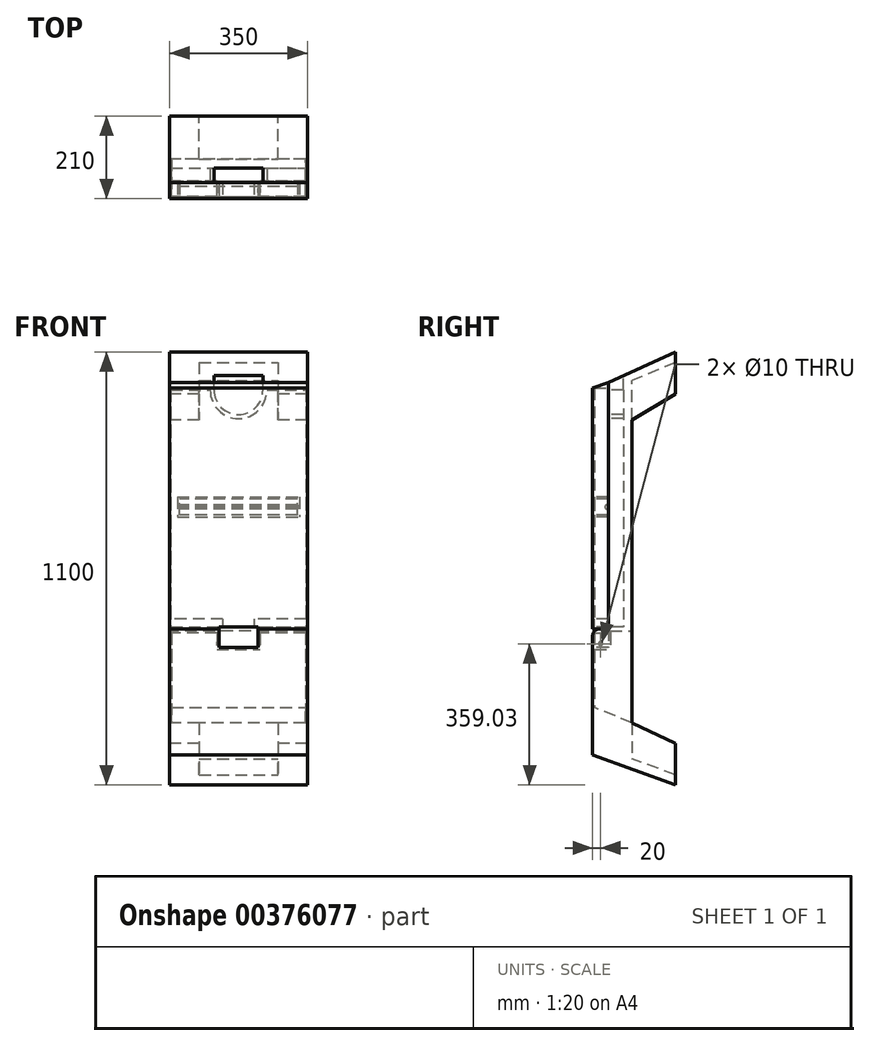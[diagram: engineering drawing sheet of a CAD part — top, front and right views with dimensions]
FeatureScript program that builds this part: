
annotation { "Feature Type Name" : "Feature", "Feature Type Description" : "" }
export const myFeature = defineFeature(function(context is Context, id is Id, definition is map)
    precondition{}
    {
        {
            var Q0;
            Q0=qCreatedBy(makeId("Front.planeOp"),FACE);
            var sketch = newSketch(context, id + "F0", { "sketchPlane" : qUnion([Q0])});
            skLineSegment(sketch, "E0.bottom", {"start": v(175, -310) * mm, "end": v(-175, -310) * mm});
            skLineSegment(sketch, "E0.top", {"start": v(175, 364) * mm, "end": v(-175, 364) * mm});
            skLineSegment(sketch, "E0.left", {"start": v(175, -310) * mm, "end": v(175, 364) * mm});
            skLineSegment(sketch, "E0.right", {"start": v(-175, -310) * mm, "end": v(-175, 364) * mm});
            skSolve(sketch);
        }
        {
            var Q0;
            Q0=makeQuery(id+"F0.imprint","IMPRINT",FACE,{"disambiguationData":[TD([[makeQuery(id+"F0.imprint","IMPRINT",EDGE,{"derivedFrom":sQuery(id+"F0.wireOp",EDGE,"E0.bottom")}),-1.0]])]});
            extrude(context, id + "F1", {"entities" : qUnion([Q0]), "depth" : 40 * mm});
        }
        {
            var Q0;
            Q0=makeQuery(id+"F1.opExtrude","CAP_FACE",FACE,{"disambiguationData":[OSD([sQuery(id+"F0.wireOp",EDGE,"E0.bottom"),sQuery(id+"F0.wireOp",EDGE,"E0.top"),sQuery(id+"F0.wireOp",EDGE,"E0.left"),sQuery(id+"F0.wireOp",EDGE,"E0.right")])],"isStart":true});
            var sketch = newSketch(context, id + "F2", { "sketchPlane" : qUnion([Q0])});
            skLineSegment(sketch, "E1.bottom", {"start": v(-172, 349) * mm, "end": v(172, 349) * mm});
            skLineSegment(sketch, "E1.top", {"start": v(-172, -237.6) * mm, "end": v(172, -237.6) * mm});
            skLineSegment(sketch, "E1.left", {"start": v(-172, 349) * mm, "end": v(-172, -237.6) * mm});
            skLineSegment(sketch, "E1.right", {"start": v(172, 349) * mm, "end": v(172, -237.6) * mm});
            skSolve(sketch);
        }
        {
            var Q0;
            Q0 = qSketchRegion(id + "F2", true);
            extrude(context, id + "F3", {"entities" : qUnion([Q0]), "operationType" : NewBodyOperationType.REMOVE, "oppositeDirection" : true, "depth" : 36 * mm});
        }
        {
            var Q0;
            Q0=makeQuery(id+"F3.boolean.opBoolean","COPY",FACE,{"derivedFrom":makeQuery(id+"F3.opExtrude","CAP_FACE",FACE,{"disambiguationData":[OSD([sQuery(id+"F2.wireOp",EDGE,"E1.bottom"),sQuery(id+"F2.wireOp",EDGE,"E1.top"),sQuery(id+"F2.wireOp",EDGE,"E1.left"),sQuery(id+"F2.wireOp",EDGE,"E1.right")])],"isStart":false})});
            var sketch = newSketch(context, id + "F4", { "sketchPlane" : qUnion([Q0])});
            skLineSegment(sketch, "E2.bottom", {"start": v(155, 72.4) * mm, "end": v(-155, 72.4) * mm});
            skLineSegment(sketch, "E2.top", {"start": v(155, 22.4) * mm, "end": v(-155, 22.4) * mm});
            skLineSegment(sketch, "E2.left", {"start": v(155, 72.4) * mm, "end": v(155, 22.4) * mm});
            skLineSegment(sketch, "E2.right", {"start": v(-155, 72.4) * mm, "end": v(-155, 22.4) * mm});
            skLineSegment(sketch, "E3.bottom", {"start": v(150, 67.4) * mm, "end": v(-150, 67.4) * mm});
            skLineSegment(sketch, "E3.top", {"start": v(150, 27.4) * mm, "end": v(-150, 27.4) * mm});
            skLineSegment(sketch, "E3.left", {"start": v(150, 67.4) * mm, "end": v(150, 27.4) * mm});
            skLineSegment(sketch, "E3.right", {"start": v(-150, 67.4) * mm, "end": v(-150, 27.4) * mm});
            skSolve(sketch);
        }
        {
            var Q0;
            Q0 = qSketchRegion(id + "F4", true);
            extrude(context, id + "F5", {"entities" : qUnion([Q0]), "operationType" : NewBodyOperationType.ADD, "depth" : 37 * mm});
        }
        {
            var Q0;
            Q0=qCreatedBy(makeId("Right.planeOp"),FACE);
            var sketch = newSketch(context, id + "F6", { "sketchPlane" : qUnion([Q0])});
            skCircle(sketch, "E4", {"center": v(-4, 47.4) * mm, "radius": 5 * mm});
            skSolve(sketch);
        }
        {
            var Q0;
            Q0 = qSketchRegion(id + "F6", true);
            extrude(context, id + "F7", {"entities" : qUnion([Q0]), "endBound" : BoundingType.SYMMETRIC, "depth" : 300 * mm});
        }
        {
            var Q0;
            Q0=makeQuery(id+"F1.opExtrude","CAP_FACE",FACE,{"disambiguationData":[OSD([sQuery(id+"F0.wireOp",EDGE,"E0.bottom"),sQuery(id+"F0.wireOp",EDGE,"E0.top"),sQuery(id+"F0.wireOp",EDGE,"E0.left"),sQuery(id+"F0.wireOp",EDGE,"E0.right")])],"isStart":true});
            var sketch = newSketch(context, id + "F8", { "sketchPlane" : qUnion([Q0])});
            skLineSegment(sketch, "E5.bottom", {"start": v(-175, -262.6) * mm, "end": v(-50, -262.6) * mm});
            skLineSegment(sketch, "E5.top", {"start": v(-175, -342.73) * mm, "end": v(-50, -342.73) * mm});
            skLineSegment(sketch, "E5.left", {"start": v(-175, -262.6) * mm, "end": v(-175, -342.73) * mm});
            skLineSegment(sketch, "E5.right", {"start": v(-50, -262.6) * mm, "end": v(-50, -342.73) * mm});
            skLineSegment(sketch, "E6.bottom", {"start": v(175, -262.6) * mm, "end": v(50, -262.6) * mm});
            skLineSegment(sketch, "E6.top", {"start": v(175, -338.6) * mm, "end": v(50, -338.6) * mm});
            skLineSegment(sketch, "E6.left", {"start": v(175, -262.6) * mm, "end": v(175, -338.6) * mm});
            skLineSegment(sketch, "E6.right", {"start": v(50, -262.6) * mm, "end": v(50, -338.6) * mm});
            skSolve(sketch);
        }
        {
            var Q0;
            Q0 = qSketchRegion(id + "F8", true);
            extrude(context, id + "F9", {"entities" : qUnion([Q0]), "operationType" : NewBodyOperationType.REMOVE, "endBound" : BoundingType.THROUGH_ALL, "oppositeDirection" : true, "depth" : 25 * mm});
        }
        {
            var Q0;
            Q0=makeQuery(id+"F1.opExtrude","CAP_EDGE",EDGE,{"disambiguationData":[OSD([sQuery(id+"F0.wireOp",EDGE,"E0.bottom")])],"isStart":true});
            fillet(context, id + "F10", {"entities" : qUnion([Q0]), "radius" : 20 * mm, "tangentPropagation" : true, "allowEdgeOverflow" : false});
        }
        {
            var Q0;
            Q0=makeQuery(id+"F9.boolean.opBoolean","COPY",FACE,{"derivedFrom":makeQuery(id+"F9.opExtrude","SWEPT_FACE",FACE,{"disambiguationData":[OSD([sQuery(id+"F8.wireOp",EDGE,"E5.right")])]})});
            var sketch = newSketch(context, id + "F11", { "sketchPlane" : qUnion([Q0])});
            skCircle(sketch, "E7", {"center": v(-20, -300) * mm, "radius": 5 * mm});
            skSolve(sketch);
        }
        {
            var Q0;
            Q0 = qSketchRegion(id + "F11", true);
            extrude(context, id + "F12", {"entities" : qUnion([Q0]), "operationType" : NewBodyOperationType.ADD, "depth" : 25 * mm});
        }
        {
            var Q0;
            Q0=makeQuery(id+"F9.boolean.opBoolean","COPY",FACE,{"derivedFrom":makeQuery(id+"F9.opExtrude","SWEPT_FACE",FACE,{"disambiguationData":[OSD([sQuery(id+"F8.wireOp",EDGE,"E6.right")])]})});
            var sketch = newSketch(context, id + "F13", { "sketchPlane" : qUnion([Q0])});
            skCircle(sketch, "E8.0", {"center": v(20, -300) * mm, "radius": 5 * mm});
            skSolve(sketch);
        }
        {
            var Q0;
            Q0 = qSketchRegion(id + "F13", true);
            extrude(context, id + "F14", {"entities" : qUnion([Q0]), "operationType" : NewBodyOperationType.ADD, "depth" : 25 * mm});
        }
        {
            var Q0;
            Q0=makeQuery(id+"F1.opExtrude","SWEPT_FACE",FACE,{"disambiguationData":[OSD([sQuery(id+"F0.wireOp",EDGE,"E0.right")])]});
            var sketch = newSketch(context, id + "F15", { "sketchPlane" : qUnion([Q0])});
            skLineSegment(sketch, "E9", {"start": v(0, 364) * mm, "end": v(40, 349) * mm});
            skLineSegment(sketch, "E10.0", {"start": v(40, 364) * mm, "end": v(0, 364) * mm});
            skLineSegment(sketch, "E11.0", {"start": v(40, 349) * mm, "end": v(40, 364) * mm});
            skPoint(sketch, "E12.orphan", {"position": v(40, -262.6) * mm});
            skSolve(sketch);
        }
        {
            var Q0;
            Q0 = qSketchRegion(id + "F15", true);
            extrude(context, id + "F16", {"entities" : qUnion([Q0]), "operationType" : NewBodyOperationType.REMOVE, "endBound" : BoundingType.THROUGH_ALL, "oppositeDirection" : true, "depth" : 25 * mm});
        }
        {
            var Q0;
            Q0=makeQuery(id+"F1.opExtrude","CAP_FACE",FACE,{"disambiguationData":[OSD([sQuery(id+"F0.wireOp",EDGE,"E0.bottom"),sQuery(id+"F0.wireOp",EDGE,"E0.top"),sQuery(id+"F0.wireOp",EDGE,"E0.left"),sQuery(id+"F0.wireOp",EDGE,"E0.right")])],"isStart":true});
            var sketch = newSketch(context, id + "F17", { "sketchPlane" : qUnion([Q0])});
            skLineSegment(sketch, "E13.bottom", {"start": v(-40, -195.53) * mm, "end": v(40, -195.53) * mm});
            skLineSegment(sketch, "E13.top", {"start": v(-40, -275) * mm, "end": v(40, -275) * mm});
            skLineSegment(sketch, "E13.left", {"start": v(-40, -195.53) * mm, "end": v(-40, -275) * mm});
            skLineSegment(sketch, "E13.right", {"start": v(40, -195.53) * mm, "end": v(40, -275) * mm});
            skSolve(sketch);
        }
        {
            var Q0;
            Q0 = qSketchRegion(id + "F17", true);
            var Q1;
            {var subQ0=sQuery(id+"F2.wireOp",EDGE,"E1.right");var subQ1=sQuery(id+"F2.wireOp",EDGE,"E1.left");var subQ2=sQuery(id+"F2.wireOp",EDGE,"E1.top");var subQ3=sQuery(id+"F2.wireOp",EDGE,"E1.bottom");Q1=makeQuery(id+"F5.boolean.opBoolean","SPLIT",FACE,{"disambiguationData":[TD([makeQuery(id+"F3.boolean.opBoolean","COPY",FACE,{"derivedFrom":makeQuery(id+"F3.opExtrude","SWEPT_FACE",FACE,{"disambiguationData":[OSD([subQ3])]})})])],"derivedFrom":makeQuery(id+"F3.boolean.opBoolean","COPY",FACE,{"derivedFrom":makeQuery(id+"F3.opExtrude","CAP_FACE",FACE,{"disambiguationData":[OSD([subQ3,subQ2,subQ1,subQ0])],"isStart":false})})});}
            extrude(context, id + "F18", {"entities" : qUnion([Q0]), "operationType" : NewBodyOperationType.REMOVE, "endBound" : BoundingType.UP_TO_SURFACE, "oppositeDirection" : true, "endBoundEntityFace" : qUnion([Q1]), "depth" : 25 * mm});
        }
        {
            var Q0;
            Q0=qCreatedBy(makeId("Right.planeOp"),FACE);
            var sketch = newSketch(context, id + "F19", { "sketchPlane" : qUnion([Q0])});
            skPoint(sketch, "E14.0", {"position": v(-40, -310) * mm});
            skPoint(sketch, "E15.0", {"position": v(-40, -262.6) * mm});
            skPoint(sketch, "E16.0", {"position": v(0, -262.6) * mm});
            skPoint(sketch, "E17.0", {"position": v(0, 364) * mm});
            skLineSegment(sketch, "E18", {"start": v(170, -659.03) * mm, "end": v(-40, -582.6) * mm});
            skLineSegment(sketch, "E19", {"start": v(-40, -582.6) * mm, "end": v(-40, -262.6) * mm});
            skLineSegment(sketch, "E20", {"start": v(0, -262.6) * mm, "end": v(-40, -262.6) * mm});
            skLineSegment(sketch, "E21", {"start": v(0, -262.6) * mm, "end": v(0, 364) * mm});
            skLineSegment(sketch, "E22", {"start": v(0, 364) * mm, "end": v(170, 440.97) * mm});
            skLineSegment(sketch, "E23", {"start": v(170, 440.97) * mm, "end": v(170, 334.97) * mm});
            skLineSegment(sketch, "E24", {"start": v(170, 334.97) * mm, "end": v(60, 268.26) * mm});
            skLineSegment(sketch, "E25", {"start": v(60, 268.26) * mm, "end": v(60, -501.74) * mm});
            skLineSegment(sketch, "E26", {"start": v(60, -501.74) * mm, "end": v(170, -553.03) * mm});
            skLineSegment(sketch, "E27", {"start": v(170, -553.03) * mm, "end": v(170, -659.03) * mm});
            skSolve(sketch);
        }
        {
            var Q0;
            Q0=makeQuery(id+"F19.imprint","IMPRINT",FACE,{"disambiguationData":[TD([[makeQuery(id+"F19.imprint","IMPRINT",EDGE,{"derivedFrom":sQuery(id+"F19.wireOp",EDGE,"E18")}),-1.0]])]});
            extrude(context, id + "F20", {"entities" : qUnion([Q0]), "endBound" : BoundingType.SYMMETRIC, "depth" : 350 * mm});
        }
        {
            var Q0;
            Q0=makeQuery(id+"F20.opExtrude","SWEPT_FACE",FACE,{"disambiguationData":[OSD([sQuery(id+"F19.wireOp",EDGE,"E21")])]});
            var sketch = newSketch(context, id + "F21", { "sketchPlane" : qUnion([Q0])});
            skLineSegment(sketch, "E28.bottom", {"start": v(-172, 344) * mm, "end": v(-72, 344) * mm});
            skLineSegment(sketch, "E28.top", {"start": v(-172, -257.6) * mm, "end": v(172, -257.6) * mm});
            skLineSegment(sketch, "E28.left", {"start": v(-172, 344) * mm, "end": v(-172, -257.6) * mm});
            skLineSegment(sketch, "E28.right", {"start": v(172, 344) * mm, "end": v(172, -257.6) * mm});
            skArc(sketch, "E29", {"start": v(-72, 344) * mm, "mid": v(0, 272) * mm, "end": v(72, 344) * mm});
            skLineSegment(sketch, "E30.trimOffspring", {"start": v(72, 344) * mm, "end": v(172, 344) * mm});
            skSolve(sketch);
        }
        {
            var Q0;
            Q0 = qSketchRegion(id + "F21", true);
            extrude(context, id + "F22", {"entities" : qUnion([Q0]), "operationType" : NewBodyOperationType.REMOVE, "oppositeDirection" : true, "depth" : 38 * mm});
        }
        {
            var Q0;
            Q0=makeQuery(id+"F20.opExtrude","SWEPT_FACE",FACE,{"disambiguationData":[OSD([sQuery(id+"F19.wireOp",EDGE,"E21")])]});
            var sketch = newSketch(context, id + "F23", { "sketchPlane" : qUnion([Q0])});
            skPoint(sketch, "E31.0", {"position": v(72, 344) * mm});
            skPoint(sketch, "E31.1", {"position": v(-72, 344) * mm});
            skArc(sketch, "E32", {"start": v(-62, 344) * mm, "mid": v(0, 282) * mm, "end": v(62, 344) * mm});
            skLineSegment(sketch, "E33.top", {"start": v(62, 388.11) * mm, "end": v(-62, 388.11) * mm});
            skLineSegment(sketch, "E33.left", {"start": v(62, 344) * mm, "end": v(62, 388.11) * mm});
            skLineSegment(sketch, "E33.right", {"start": v(-62, 344) * mm, "end": v(-62, 388.11) * mm});
            skSolve(sketch);
        }
        {
            var Q0;
            Q0 = qSketchRegion(id + "F23", true);
            extrude(context, id + "F24", {"entities" : qUnion([Q0]), "operationType" : NewBodyOperationType.REMOVE, "oppositeDirection" : true, "depth" : 38 * mm});
        }
        {
            var Q0;
            Q0=qCreatedBy(makeId("Right.planeOp"),FACE);
            var sketch = newSketch(context, id + "F25", { "sketchPlane" : qUnion([Q0])});
            skLineSegment(sketch, "E34.0", {"start": v(170, -553.03) * mm, "end": v(170, -633.03) * mm});
            skLineSegment(sketch, "E35", {"start": v(170, -633.03) * mm, "end": v(60, -593) * mm});
            skPoint(sketch, "E36.0", {"position": v(60, -501.74) * mm});
            skLineSegment(sketch, "E37", {"start": v(60, -501.74) * mm, "end": v(60, -593) * mm});
            skLineSegment(sketch, "E38", {"start": v(170, -633.03) * mm, "end": v(170, -466.14) * mm});
            skLineSegment(sketch, "E39", {"start": v(170, -466.14) * mm, "end": v(60, -501.74) * mm});
            skPoint(sketch, "E40.0.end.orphan", {"position": v(-40, -582.6) * mm});
            skPoint(sketch, "E41.orphan", {"position": v(170, -659.03) * mm});
            skPoint(sketch, "E42.0", {"position": v(170, 440.97) * mm});
            skPoint(sketch, "E42.1", {"position": v(170, 334.97) * mm});
            skPoint(sketch, "E42.2", {"position": v(60, 268.26) * mm});
            skLineSegment(sketch, "E43.0", {"start": v(170, 414.97) * mm, "end": v(170, 334.97) * mm});
            skLineSegment(sketch, "E44", {"start": v(170, 414.97) * mm, "end": v(60, 368.4) * mm});
            skLineSegment(sketch, "E45", {"start": v(170, 414.97) * mm, "end": v(170, 214.7) * mm});
            skLineSegment(sketch, "E46", {"start": v(170, 214.7) * mm, "end": v(60, 268.26) * mm});
            skLineSegment(sketch, "E47", {"start": v(60, 268.26) * mm, "end": v(60, 368.4) * mm});
            skPoint(sketch, "E48.orphan", {"position": v(0, 364) * mm});
            skSolve(sketch);
        }
        {
            var Q0;
            Q0 = qSketchRegion(id + "F25", true);
            extrude(context, id + "F26", {"entities" : qUnion([Q0]), "operationType" : NewBodyOperationType.REMOVE, "endBound" : BoundingType.SYMMETRIC, "oppositeDirection" : true, "depth" : 200 * mm});
        }
        {
            var Q0;
            Q0=qCreatedBy(makeId("Right.planeOp"),FACE);
            var sketch = newSketch(context, id + "F27", { "sketchPlane" : qUnion([Q0])});
            skPoint(sketch, "E49.0", {"position": v(0, -257.6) * mm});
            skPoint(sketch, "E50.0", {"position": v(-40, -310) * mm});
            skLineSegment(sketch, "E51.bottom", {"start": v(0, -257.6) * mm, "end": v(-40, -257.6) * mm});
            skLineSegment(sketch, "E51.top", {"start": v(0, -310) * mm, "end": v(-40, -310) * mm});
            skLineSegment(sketch, "E51.left", {"start": v(0, -257.6) * mm, "end": v(0, -310) * mm});
            skLineSegment(sketch, "E51.right", {"start": v(-40, -257.6) * mm, "end": v(-40, -310) * mm});
            skSolve(sketch);
        }
        {
            var Q0;
            Q0 = qSketchRegion(id + "F27", true);
            extrude(context, id + "F28", {"entities" : qUnion([Q0]), "operationType" : NewBodyOperationType.REMOVE, "endBound" : BoundingType.SYMMETRIC, "oppositeDirection" : true, "depth" : 100 * mm});
        }
        {
            var Q0;
            Q0=qCreatedBy(makeId("Right.planeOp"),FACE);
            var sketch = newSketch(context, id + "F29", { "sketchPlane" : qUnion([Q0])});
            skPoint(sketch, "E52.0", {"position": v(38, -257.6) * mm});
            skPoint(sketch, "E53.0", {"position": v(0, -257.6) * mm});
            skPoint(sketch, "E54.0", {"position": v(0, -310) * mm});
            skPoint(sketch, "E55.0", {"position": v(-40, -310) * mm});
            skLineSegment(sketch, "E56.bottom", {"start": v(5, -267.6) * mm, "end": v(81.3, -267.6) * mm});
            skLineSegment(sketch, "E56.left", {"start": v(5, -267.6) * mm, "end": v(5, -315) * mm});
            skLineSegment(sketch, "E56.right", {"start": v(81.3, -267.6) * mm, "end": v(81.3, -331.9) * mm});
            skLineSegment(sketch, "E57.0", {"start": v(-40, -310) * mm, "end": v(-40, -262.6) * mm});
            skLineSegment(sketch, "E58.bottom", {"start": v(-35, -315) * mm, "end": v(5, -315) * mm});
            skLineSegment(sketch, "E58.left", {"start": v(-35, -315) * mm, "end": v(-35, -462.44) * mm});
            skLineSegment(sketch, "E59", {"start": v(60, -501.74) * mm, "end": v(-35, -462.44) * mm});
            skPoint(sketch, "E60.orphan", {"position": v(-40, -582.6) * mm});
            skLineSegment(sketch, "E61", {"start": v(60, -501.74) * mm, "end": v(81.3, -331.9) * mm});
            skSolve(sketch);
        }
        {
            var Q0;
            Q0 = qSketchRegion(id + "F29", true);
            extrude(context, id + "F30", {"entities" : qUnion([Q0]), "operationType" : NewBodyOperationType.REMOVE, "endBound" : BoundingType.SYMMETRIC, "oppositeDirection" : true, "depth" : 340 * mm});
        }
        {
            var Q0;
            Q0=makeQuery(id+"F30.boolean.opBoolean","COPY",FACE,{"derivedFrom":makeQuery(id+"F30.opExtrude","SWEPT_FACE",FACE,{"disambiguationData":[OSD([sQuery(id+"F29.wireOp",EDGE,"E56.left")])]})});
            var sketch = newSketch(context, id + "F31", { "sketchPlane" : qUnion([Q0])});
            skPoint(sketch, "E62.0", {"position": v(-170, -267.6) * mm});
            skPoint(sketch, "E63.0", {"position": v(-170, -315) * mm});
            skLineSegment(sketch, "E64.top", {"start": v(-170, -315) * mm, "end": v(-55, -315) * mm});
            skLineSegment(sketch, "E64.left", {"start": v(-170, -272.6) * mm, "end": v(-170, -315) * mm});
            skLineSegment(sketch, "E64.right", {"start": v(-55, -272.6) * mm, "end": v(-55, -315) * mm});
            skPoint(sketch, "E65.0", {"position": v(170, -267.6) * mm});
            skPoint(sketch, "E65.1", {"position": v(170, -315) * mm});
            skLineSegment(sketch, "E66.top", {"start": v(170, -315) * mm, "end": v(55, -315) * mm});
            skLineSegment(sketch, "E66.left", {"start": v(170, -272.6) * mm, "end": v(170, -315) * mm});
            skLineSegment(sketch, "E66.right", {"start": v(55, -272.6) * mm, "end": v(55, -315) * mm});
            skLineSegment(sketch, "E67", {"start": v(55, -272.6) * mm, "end": v(170, -272.6) * mm});
            skLineSegment(sketch, "E68", {"start": v(-170, -272.6) * mm, "end": v(-55, -272.6) * mm});
            skSolve(sketch);
        }
        {
            var Q0;
            Q0 = qSketchRegion(id + "F31", true);
            var Q1;
            Q1=makeQuery(id+"F30.boolean.opBoolean","COPY",FACE,{"derivedFrom":makeQuery(id+"F30.opExtrude","SWEPT_FACE",FACE,{"disambiguationData":[OSD([sQuery(id+"F29.wireOp",EDGE,"E58.left")])]})});
            extrude(context, id + "F32", {"entities" : qUnion([Q0]), "operationType" : NewBodyOperationType.REMOVE, "endBound" : BoundingType.UP_TO_SURFACE, "oppositeDirection" : true, "endBoundEntityFace" : qUnion([Q1]), "depth" : 25 * mm});
        }
        {
            var Q0;
            Q0=makeQuery(id+"F32.boolean.opBoolean","COPY",FACE,{"derivedFrom":makeQuery(id+"F32.opExtrude","SWEPT_FACE",FACE,{"disambiguationData":[OSD([sQuery(id+"F31.wireOp",EDGE,"E64.right")])]})});
            var sketch = newSketch(context, id + "F33", { "sketchPlane" : qUnion([Q0])});
            skCircle(sketch, "E69.0.0", {"center": v(-20, -300) * mm, "radius": 5 * mm});
            skSolve(sketch);
        }
        {
            var Q0;
            Q0 = qSketchRegion(id + "F33", true);
            extrude(context, id + "F34", {"entities" : qUnion([Q0]), "operationType" : NewBodyOperationType.REMOVE, "oppositeDirection" : true, "depth" : 5 * mm});
        }
        {
            var Q0;
            Q0=makeQuery(id+"F32.boolean.opBoolean","COPY",FACE,{"derivedFrom":makeQuery(id+"F32.opExtrude","SWEPT_FACE",FACE,{"disambiguationData":[OSD([sQuery(id+"F31.wireOp",EDGE,"E66.right")])]})});
            var sketch = newSketch(context, id + "F35", { "sketchPlane" : qUnion([Q0])});
            skCircle(sketch, "E70.0", {"center": v(20, -300) * mm, "radius": 5 * mm});
            skSolve(sketch);
        }
        {
            var Q0;
            Q0 = qSketchRegion(id + "F35", true);
            extrude(context, id + "F36", {"entities" : qUnion([Q0]), "operationType" : NewBodyOperationType.REMOVE, "oppositeDirection" : true, "depth" : 5 * mm});
        }
        {
            var Q0;
            {var subQ0=sQuery(id+"F19.wireOp",EDGE,"E20");var subQ1=sQuery(id+"F19.wireOp",EDGE,"E19");Q0=makeQuery(id+"F28.boolean.opBoolean","SPLIT",EDGE,{"disambiguationData":[TD([makeQuery(id+"F28.opExtrude","CAP_FACE",FACE,{"disambiguationData":[OSD([sQuery(id+"F27.wireOp",EDGE,"E51.bottom"),sQuery(id+"F27.wireOp",EDGE,"E51.top"),sQuery(id+"F27.wireOp",EDGE,"E51.left"),sQuery(id+"F27.wireOp",EDGE,"E51.right")])],"isStart":false})])],"derivedFrom":makeQuery(id+"F20.opExtrude","SWEPT_EDGE",EDGE,{"disambiguationData":[OSD([subQ1,subQ0])]})});}
            var Q1;
            {var subQ0=sQuery(id+"F19.wireOp",EDGE,"E20");var subQ1=sQuery(id+"F19.wireOp",EDGE,"E19");Q1=makeQuery(id+"F28.boolean.opBoolean","SPLIT",EDGE,{"disambiguationData":[TD([makeQuery(id+"F28.opExtrude","CAP_FACE",FACE,{"disambiguationData":[OSD([sQuery(id+"F27.wireOp",EDGE,"E51.bottom"),sQuery(id+"F27.wireOp",EDGE,"E51.top"),sQuery(id+"F27.wireOp",EDGE,"E51.left"),sQuery(id+"F27.wireOp",EDGE,"E51.right")])],"isStart":true})])],"derivedFrom":makeQuery(id+"F20.opExtrude","SWEPT_EDGE",EDGE,{"disambiguationData":[OSD([subQ1,subQ0])]})});}
            fillet(context, id + "F37", {"entities" : qUnion([Q0, Q1]), "radius" : 17 * mm, "tangentPropagation" : true, "allowEdgeOverflow" : false});
        }
    });
